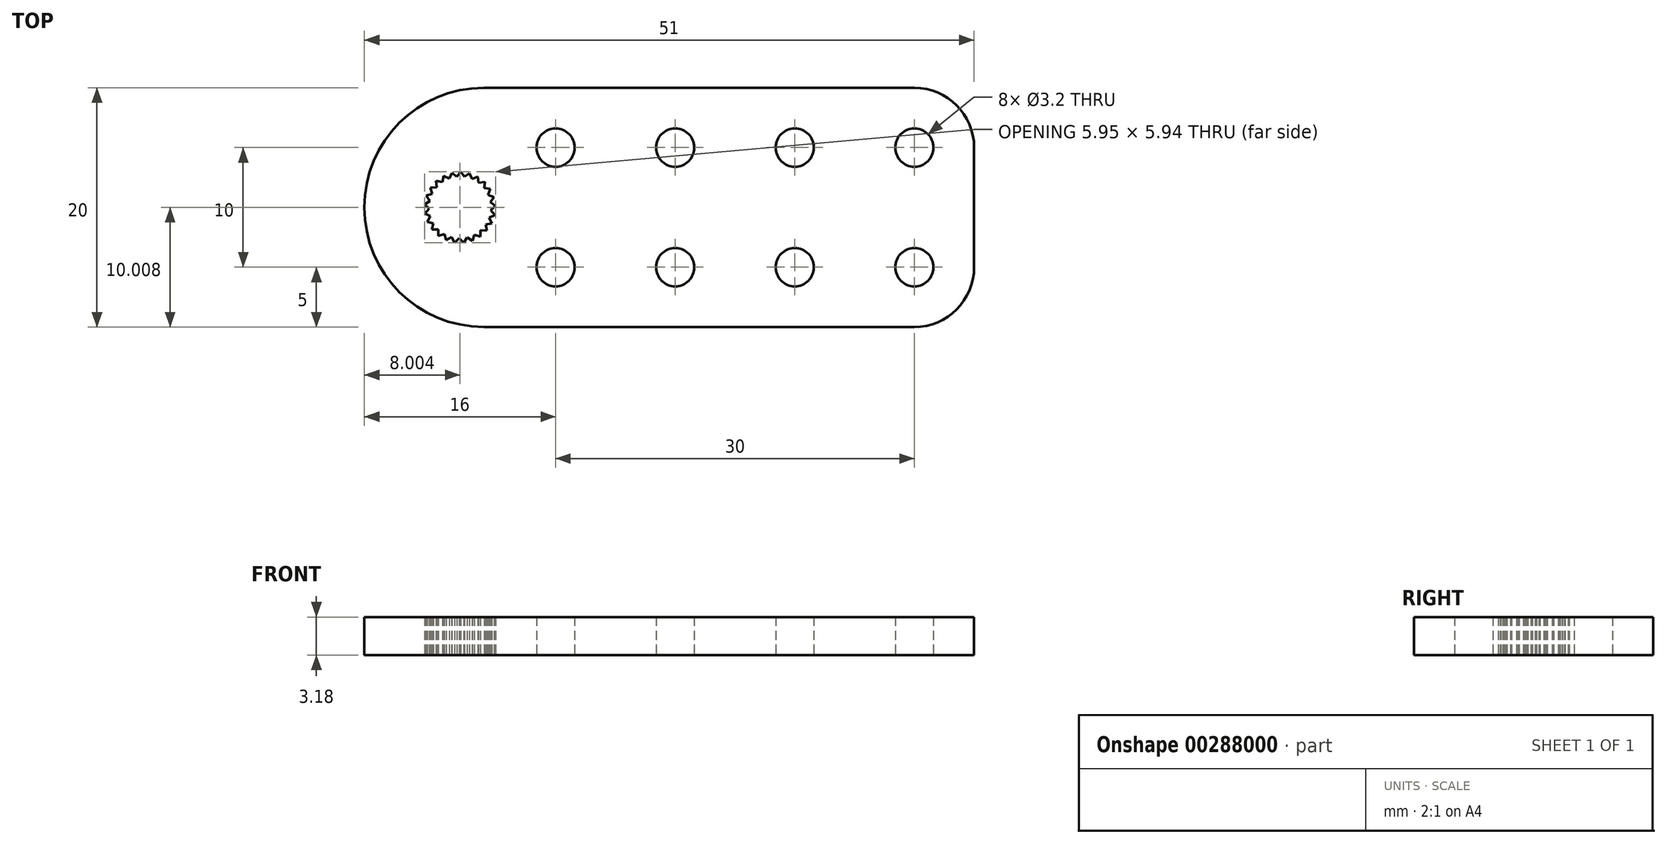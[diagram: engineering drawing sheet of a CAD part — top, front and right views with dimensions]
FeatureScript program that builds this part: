
annotation { "Feature Type Name" : "Feature", "Feature Type Description" : "" }
export const myFeature = defineFeature(function(context is Context, id is Id, definition is map)
    precondition{}
    {
        {
            var Q0;
            Q0=qCreatedBy(makeId("Top.planeOp"),FACE);
            var sketch = newSketch(context, id + "F0", { "sketchPlane" : qUnion([Q0])});
            skLineSegment(sketch, "E0.bottom", {"start": v(10, 0) * mm, "end": v(46, 0) * mm});
            skLineSegment(sketch, "E0.top", {"start": v(10, 20) * mm, "end": v(46, 20) * mm});
            skLineSegment(sketch, "E0.right", {"start": v(51, 5) * mm, "end": v(51, 15) * mm});
            skCircle(sketch, "E1", {"center": v(46, 15) * mm, "radius": 1.6 * mm});
            skCircle(sketch, "E2.0.1.0", {"center": v(46, 5) * mm, "radius": 1.6 * mm});
            skCircle(sketch, "E2.1.0.0", {"center": v(36, 15) * mm, "radius": 1.6 * mm});
            skCircle(sketch, "E2.1.1.0", {"center": v(36, 5) * mm, "radius": 1.6 * mm});
            skCircle(sketch, "E2.2.0.0", {"center": v(26, 15) * mm, "radius": 1.6 * mm});
            skCircle(sketch, "E2.2.1.0", {"center": v(26, 5) * mm, "radius": 1.6 * mm});
            skCircle(sketch, "E2.3.0.0", {"center": v(16, 15) * mm, "radius": 1.6 * mm});
            skCircle(sketch, "E2.3.1.0", {"center": v(16, 5) * mm, "radius": 1.6 * mm});
            skLineSegment(sketch, "E2.direction1", {"start": v(46, 15) * mm, "end": v(36, 15) * mm, "construction": true});
            skLineSegment(sketch, "E2.direction2", {"start": v(46, 15) * mm, "end": v(46, 5) * mm, "construction": true});
            skLineSegment(sketch, "E3", {"start": v(5.52, 11.65) * mm, "end": v(5.69, 11.15) * mm});
            skLineSegment(sketch, "E4", {"start": v(5.69, 11.15) * mm, "end": v(5.19, 10.98) * mm});
            skLineSegment(sketch, "E5.1.0", {"start": v(5.19, 10.98) * mm, "end": v(5.47, 10.54) * mm});
            skLineSegment(sketch, "E5.1.1", {"start": v(5.47, 10.54) * mm, "end": v(5.03, 10.25) * mm});
            skLineSegment(sketch, "E5.2.0", {"start": v(5.03, 10.25) * mm, "end": v(5.42, 9.9) * mm});
            skLineSegment(sketch, "E5.2.1", {"start": v(5.42, 9.9) * mm, "end": v(5.06, 9.5) * mm});
            skLineSegment(sketch, "E5.3.0", {"start": v(5.06, 9.5) * mm, "end": v(5.53, 9.26) * mm});
            skLineSegment(sketch, "E5.3.1", {"start": v(5.53, 9.26) * mm, "end": v(5.28, 8.8) * mm});
            skLineSegment(sketch, "E5.4.0", {"start": v(5.28, 8.8) * mm, "end": v(5.79, 8.66) * mm});
            skLineSegment(sketch, "E5.4.1", {"start": v(5.79, 8.66) * mm, "end": v(5.66, 8.15) * mm});
            skLineSegment(sketch, "E5.5.0", {"start": v(5.66, 8.15) * mm, "end": v(6.2, 8.16) * mm});
            skLineSegment(sketch, "E5.5.1", {"start": v(6.2, 8.16) * mm, "end": v(6.2, 7.63) * mm});
            skLineSegment(sketch, "E5.6.0", {"start": v(6.2, 7.63) * mm, "end": v(6.7, 7.76) * mm});
            skLineSegment(sketch, "E5.6.1", {"start": v(6.7, 7.76) * mm, "end": v(6.84, 7.25) * mm});
            skLineSegment(sketch, "E5.7.0", {"start": v(6.84, 7.25) * mm, "end": v(7.3, 7.51) * mm});
            skLineSegment(sketch, "E5.7.1", {"start": v(7.3, 7.51) * mm, "end": v(7.56, 7.05) * mm});
            skLineSegment(sketch, "E5.8.0", {"start": v(7.56, 7.05) * mm, "end": v(7.94, 7.42) * mm});
            skLineSegment(sketch, "E5.8.1", {"start": v(7.94, 7.42) * mm, "end": v(8.3, 7.04) * mm});
            skLineSegment(sketch, "E5.9.0", {"start": v(8.3, 7.04) * mm, "end": v(8.59, 7.48) * mm});
            skLineSegment(sketch, "E5.9.1", {"start": v(8.59, 7.48) * mm, "end": v(9.04, 7.2) * mm});
            skLineSegment(sketch, "E5.10.0", {"start": v(9.04, 7.2) * mm, "end": v(9.2, 7.7) * mm});
            skLineSegment(sketch, "E5.10.1", {"start": v(9.2, 7.7) * mm, "end": v(9.7, 7.55) * mm});
            skLineSegment(sketch, "E5.11.0", {"start": v(9.7, 7.55) * mm, "end": v(9.73, 8.08) * mm});
            skLineSegment(sketch, "E5.11.1", {"start": v(9.73, 8.08) * mm, "end": v(10.25, 8.05) * mm});
            skLineSegment(sketch, "E5.12.0", {"start": v(10.25, 8.05) * mm, "end": v(10.15, 8.57) * mm});
            skLineSegment(sketch, "E5.12.1", {"start": v(10.15, 8.57) * mm, "end": v(10.67, 8.67) * mm});
            skLineSegment(sketch, "E5.13.0", {"start": v(10.67, 8.67) * mm, "end": v(10.44, 9.15) * mm});
            skLineSegment(sketch, "E5.13.1", {"start": v(10.44, 9.15) * mm, "end": v(10.91, 9.38) * mm});
            skLineSegment(sketch, "E5.14.0", {"start": v(10.91, 9.38) * mm, "end": v(10.57, 9.78) * mm});
            skLineSegment(sketch, "E5.14.1", {"start": v(10.57, 9.78) * mm, "end": v(10.98, 10.12) * mm});
            skLineSegment(sketch, "E5.15.0", {"start": v(10.98, 10.12) * mm, "end": v(10.55, 10.43) * mm});
            skLineSegment(sketch, "E5.15.1", {"start": v(10.55, 10.43) * mm, "end": v(10.85, 10.86) * mm});
            skLineSegment(sketch, "E5.16.0", {"start": v(10.85, 10.86) * mm, "end": v(10.36, 11.05) * mm});
            skLineSegment(sketch, "E5.16.1", {"start": v(10.36, 11.05) * mm, "end": v(10.55, 11.54) * mm});
            skLineSegment(sketch, "E5.17.0", {"start": v(10.55, 11.54) * mm, "end": v(10.03, 11.6) * mm});
            skLineSegment(sketch, "E5.17.1", {"start": v(10.03, 11.6) * mm, "end": v(10.09, 12.13) * mm});
            skLineSegment(sketch, "E5.18.0", {"start": v(10.09, 12.13) * mm, "end": v(9.56, 12.06) * mm});
            skLineSegment(sketch, "E5.18.1", {"start": v(9.56, 12.06) * mm, "end": v(9.5, 12.58) * mm});
            skLineSegment(sketch, "E5.19.0", {"start": v(9.5, 12.58) * mm, "end": v(9, 12.38) * mm});
            skLineSegment(sketch, "E5.19.1", {"start": v(9, 12.38) * mm, "end": v(8.8, 12.87) * mm});
            skLineSegment(sketch, "E5.20.0", {"start": v(8.8, 12.87) * mm, "end": v(8.38, 12.56) * mm});
            skLineSegment(sketch, "E5.20.1", {"start": v(8.38, 12.56) * mm, "end": v(8.07, 12.98) * mm});
            skLineSegment(sketch, "E5.21.0", {"start": v(8.07, 12.98) * mm, "end": v(7.73, 12.57) * mm});
            skLineSegment(sketch, "E5.21.1", {"start": v(7.73, 12.57) * mm, "end": v(7.32, 12.9) * mm});
            skLineSegment(sketch, "E5.22.0", {"start": v(7.32, 12.9) * mm, "end": v(7.1, 12.42) * mm});
            skLineSegment(sketch, "E5.22.1", {"start": v(7.1, 12.42) * mm, "end": v(6.62, 12.64) * mm});
            skLineSegment(sketch, "E5.23.0", {"start": v(6.62, 12.64) * mm, "end": v(6.53, 12.12) * mm});
            skLineSegment(sketch, "E5.23.1", {"start": v(6.53, 12.12) * mm, "end": v(6, 12.22) * mm});
            skLineSegment(sketch, "E5.24.0", {"start": v(6, 12.22) * mm, "end": v(6.05, 11.69) * mm});
            skLineSegment(sketch, "E5.24.1", {"start": v(6.05, 11.69) * mm, "end": v(5.52, 11.65) * mm});
            skPoint(sketch, "E5.center", {"position": v(8, 10) * mm});
            skArc(sketch, "E6", {"start": v(10, 20) * mm, "mid": v(2.93, 17.07) * mm, "end": v(0, 10) * mm});
            skPoint(sketch, "E7.orphan", {"position": v(0, 20) * mm});
            skArc(sketch, "E8.MirrorCS", {"start": v(10, 0) * mm, "mid": v(2.93, 2.93) * mm, "end": v(0, 10) * mm});
            skPoint(sketch, "E9.orphan", {"position": v(0, 0) * mm});
            skArc(sketch, "E10", {"start": v(51, 15) * mm, "mid": v(49.54, 18.54) * mm, "end": v(46, 20) * mm});
            skArc(sketch, "E11.MirrorCS", {"start": v(51, 5) * mm, "mid": v(49.54, 1.46) * mm, "end": v(46, 0) * mm});
            skSolve(sketch);
        }
        {
            var Q0;
            Q0=qSketchRegion(id+"F0",true);
            extrude(context, id + "F1", {"entities" : qUnion([Q0]), "depth" : 3.17 * mm});
        }
    });
